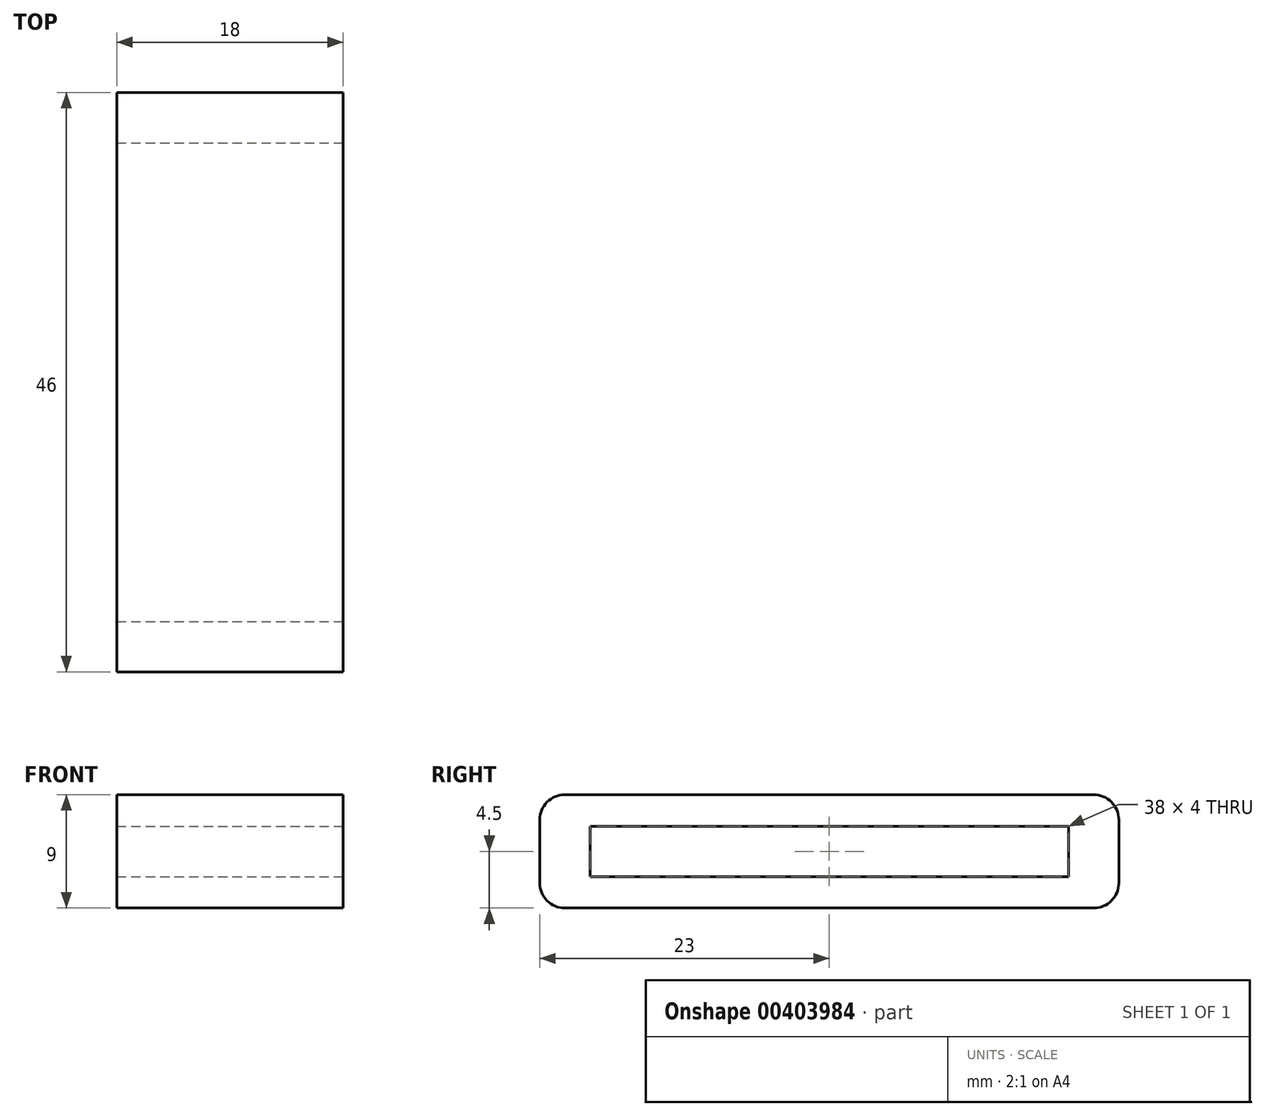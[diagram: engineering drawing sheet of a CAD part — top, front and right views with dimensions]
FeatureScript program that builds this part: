
annotation { "Feature Type Name" : "Feature", "Feature Type Description" : "" }
export const myFeature = defineFeature(function(context is Context, id is Id, definition is map)
    precondition{}
    {
        {
            var Q0;
            Q0=qCreatedBy(makeId("Top.planeOp"),FACE);
            var sketch = newSketch(context, id + "F0", { "sketchPlane" : qUnion([Q0])});
            skLineSegment(sketch, "E0.bottom", {"start": v(9, -23) * mm, "end": v(-9, -23) * mm});
            skLineSegment(sketch, "E0.top", {"start": v(9, 23) * mm, "end": v(-9, 23) * mm});
            skLineSegment(sketch, "E0.left", {"start": v(9, -23) * mm, "end": v(9, 23) * mm});
            skLineSegment(sketch, "E0.right", {"start": v(-9, -23) * mm, "end": v(-9, 23) * mm});
            skPoint(sketch, "E0.middle", {"position": v(0, 0) * mm});
            skSolve(sketch);
        }
        {
            var Q0;
            Q0 = qSketchRegion(id + "F0", true);
            extrude(context, id + "F1", {"entities" : qUnion([Q0]), "depth" : 9 * mm, "offsetDistance" : 25 * mm});
        }
        {
            var Q0;
            Q0=makeQuery(id+"F1.opExtrude","SWEPT_FACE",FACE,{"disambiguationData":[OSD([sQuery(id+"F0.wireOp",EDGE,"E0.left")])]});
            var sketch = newSketch(context, id + "F2", { "sketchPlane" : qUnion([Q0])});
            skLineSegment(sketch, "E1.bottom", {"start": v(19, 2.5) * mm, "end": v(-19, 2.5) * mm});
            skLineSegment(sketch, "E1.top", {"start": v(19, 6.5) * mm, "end": v(-19, 6.5) * mm});
            skLineSegment(sketch, "E1.left", {"start": v(19, 2.5) * mm, "end": v(19, 6.5) * mm});
            skLineSegment(sketch, "E1.right", {"start": v(-19, 2.5) * mm, "end": v(-19, 6.5) * mm});
            skPoint(sketch, "E1.middle", {"position": v(0, 4.5) * mm});
            skPoint(sketch, "E1.middle.positionSnap0", {"position": v(23, 4.5) * mm});
            skPoint(sketch, "E1.centerSnap0", {"position": v(23, 4.5) * mm});
            skSolve(sketch);
        }
        {
            var Q0;
            Q0 = qSketchRegion(id + "F2", true);
            extrude(context, id + "F3", {"entities" : qUnion([Q0]), "operationType" : NewBodyOperationType.REMOVE, "endBound" : BoundingType.THROUGH_ALL, "oppositeDirection" : true, "depth" : 25 * mm, "offsetDistance" : 25 * mm});
        }
        {
            var Q0;
            Q0=makeQuery(id+"F1.opExtrude","CAP_EDGE",EDGE,{"disambiguationData":[OSD([sQuery(id+"F0.wireOp",EDGE,"E0.bottom")])],"isStart":false});
            var Q1;
            Q1=makeQuery(id+"F1.opExtrude","CAP_EDGE",EDGE,{"disambiguationData":[OSD([sQuery(id+"F0.wireOp",EDGE,"E0.bottom")])],"isStart":true});
            var Q2;
            Q2=makeQuery(id+"F1.opExtrude","CAP_EDGE",EDGE,{"disambiguationData":[OSD([sQuery(id+"F0.wireOp",EDGE,"E0.top")])],"isStart":false});
            var Q3;
            Q3=makeQuery(id+"F1.opExtrude","CAP_EDGE",EDGE,{"disambiguationData":[OSD([sQuery(id+"F0.wireOp",EDGE,"E0.top")])],"isStart":true});
            fillet(context, id + "F4", {"entities" : qUnion([Q0, Q1, Q2, Q3]), "radius" : 2 * mm, "tangentPropagation" : true, "allowEdgeOverflow" : false});
        }
    });
